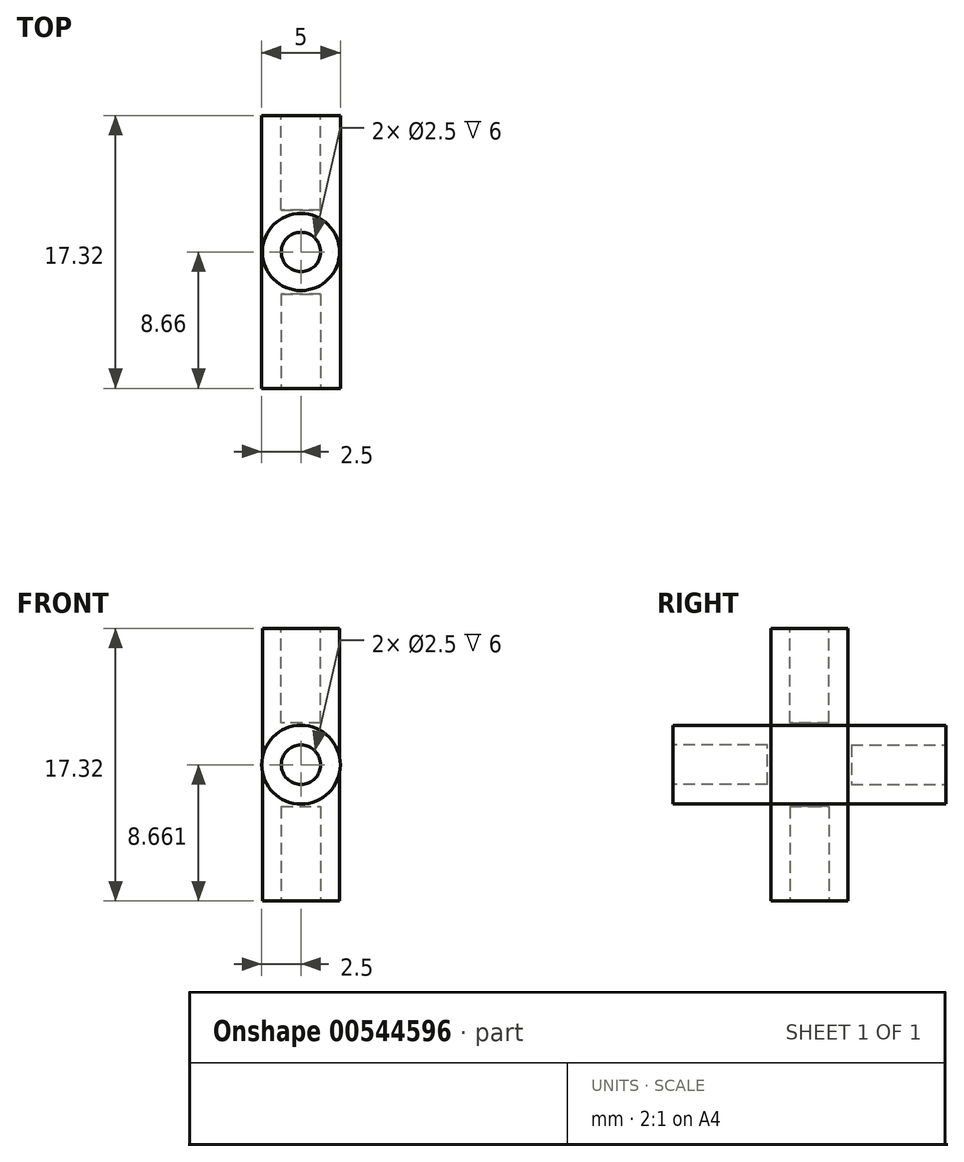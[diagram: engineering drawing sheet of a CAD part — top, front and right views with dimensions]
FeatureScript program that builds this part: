
annotation { "Feature Type Name" : "Feature", "Feature Type Description" : "" }
export const myFeature = defineFeature(function(context is Context, id is Id, definition is map)
    precondition{}
    {
        {
            var Q0;
            Q0=qCreatedBy(makeId("Top.planeOp"),FACE);
            var sketch = newSketch(context, id + "F0", { "sketchPlane" : qUnion([Q0])});
            skCircle(sketch, "E0", {"center": v(0, 0) * mm, "radius": 2.45 * mm});
            skSolve(sketch);
        }
        {
            var Q0;
            Q0=makeQuery(id+"F0.imprint","IMPRINT",FACE,{"disambiguationData":[TD([[makeQuery(id+"F0.imprint","IMPRINT",EDGE,{"derivedFrom":sQuery(id+"F0.wireOp",EDGE,"E0")}),1.0]])]});
            var Q1;
            Q1=makeQuery(id+"F0.imprint","IMPRINT",FACE,{"disambiguationData":[TD([[makeQuery(id+"F0.imprint","IMPRINT",EDGE,{"derivedFrom":sQuery(id+"F0.wireOp",EDGE,"nVHzi88V-v95H-BfBQ-eSiS-BEMK5Zbw89u3")}),1.0]])]});
            extrude(context, id + "F1", {"entities" : qUnion([Q0, Q1]), "depth" : 17.32 * mm, "offsetDistance" : 25 * mm});
        }
        {
            var Q0;
            Q0=makeQuery(id+"F1.opExtrude","CAP_FACE",FACE,{"disambiguationData":[OSD([sQuery(id+"F0.wireOp",EDGE,"E0")])],"isStart":false});
            var sketch = newSketch(context, id + "F2", { "sketchPlane" : qUnion([Q0])});
            skCircle(sketch, "E1", {"center": v(0, 0) * mm, "radius": 1.25 * mm});
            skSolve(sketch);
        }
        {
            var Q0;
            Q0=makeQuery(id+"F2.imprint","IMPRINT",FACE,{"disambiguationData":[TD([[makeQuery(id+"F2.imprint","IMPRINT",EDGE,{"derivedFrom":sQuery(id+"F2.wireOp",EDGE,"E1")}),1.0]])]});
            extrude(context, id + "F3", {"entities" : qUnion([Q0]), "operationType" : NewBodyOperationType.REMOVE, "oppositeDirection" : true, "depth" : 6 * mm, "offsetDistance" : 25 * mm});
        }
        {
            var Q0;
            Q0=qCreatedBy(makeId("Front.planeOp"),FACE);
            var sketch = newSketch(context, id + "F4", { "sketchPlane" : qUnion([Q0])});
            skCircle(sketch, "E2", {"center": v(0, 8.66) * mm, "radius": 2.5 * mm});
            skSolve(sketch);
        }
        {
            var Q0;
            Q0 = qSketchRegion(id + "F4", true);
            extrude(context, id + "F5", {"entities" : qUnion([Q0]), "depth" : 8.66 * mm, "offsetDistance" : 25 * mm, "hasSecondDirection" : true, "secondDirectionOppositeDirection" : true, "secondDirectionDepth" : 8.66 * mm});
        }
        {
            var Q0;
            Q0=makeQuery(id+"F1.opExtrude","CAP_FACE",FACE,{"disambiguationData":[OSD([sQuery(id+"F0.wireOp",EDGE,"E0")])],"isStart":true});
            var sketch = newSketch(context, id + "F6", { "sketchPlane" : qUnion([Q0])});
            skCircle(sketch, "E3", {"center": v(0, 0) * mm, "radius": 1.25 * mm});
            skSolve(sketch);
        }
        {
            var Q0;
            Q0=makeQuery(id+"F6.imprint","IMPRINT",FACE,{"disambiguationData":[TD([[makeQuery(id+"F6.imprint","IMPRINT",EDGE,{"derivedFrom":sQuery(id+"F6.wireOp",EDGE,"E3")}),1.0]])]});
            extrude(context, id + "F7", {"entities" : qUnion([Q0]), "operationType" : NewBodyOperationType.REMOVE, "oppositeDirection" : true, "depth" : 6 * mm, "offsetDistance" : 25 * mm});
        }
        {
            var Q0;
            Q0=makeQuery(id+"F5.opExtrude","CAP_FACE",FACE,{"disambiguationData":[OSD([sQuery(id+"F4.wireOp",EDGE,"E2")])],"isStart":false});
            var sketch = newSketch(context, id + "F8", { "sketchPlane" : qUnion([Q0])});
            skCircle(sketch, "E4", {"center": v(0, 8.66) * mm, "radius": 1.25 * mm});
            skSolve(sketch);
        }
        {
            var Q0;
            Q0=makeQuery(id+"F8.imprint","IMPRINT",FACE,{"disambiguationData":[TD([[makeQuery(id+"F8.imprint","IMPRINT",EDGE,{"derivedFrom":sQuery(id+"F8.wireOp",EDGE,"E4")}),1.0]])]});
            extrude(context, id + "F9", {"entities" : qUnion([Q0]), "operationType" : NewBodyOperationType.REMOVE, "oppositeDirection" : true, "depth" : 6 * mm, "offsetDistance" : 25 * mm});
        }
        {
            var Q0;
            Q0=makeQuery(id+"F5.opExtrude","CAP_FACE",FACE,{"disambiguationData":[OSD([sQuery(id+"F4.wireOp",EDGE,"E2")])],"isStart":true});
            var sketch = newSketch(context, id + "F10", { "sketchPlane" : qUnion([Q0])});
            skCircle(sketch, "E5", {"center": v(0, 8.66) * mm, "radius": 1.25 * mm});
            skSolve(sketch);
        }
        {
            var Q0;
            Q0=makeQuery(id+"F10.imprint","IMPRINT",FACE,{"disambiguationData":[TD([[makeQuery(id+"F10.imprint","IMPRINT",EDGE,{"derivedFrom":sQuery(id+"F10.wireOp",EDGE,"E5")}),1.0]])]});
            extrude(context, id + "F11", {"entities" : qUnion([Q0]), "operationType" : NewBodyOperationType.REMOVE, "oppositeDirection" : true, "depth" : 6 * mm, "offsetDistance" : 25 * mm});
        }
    });
